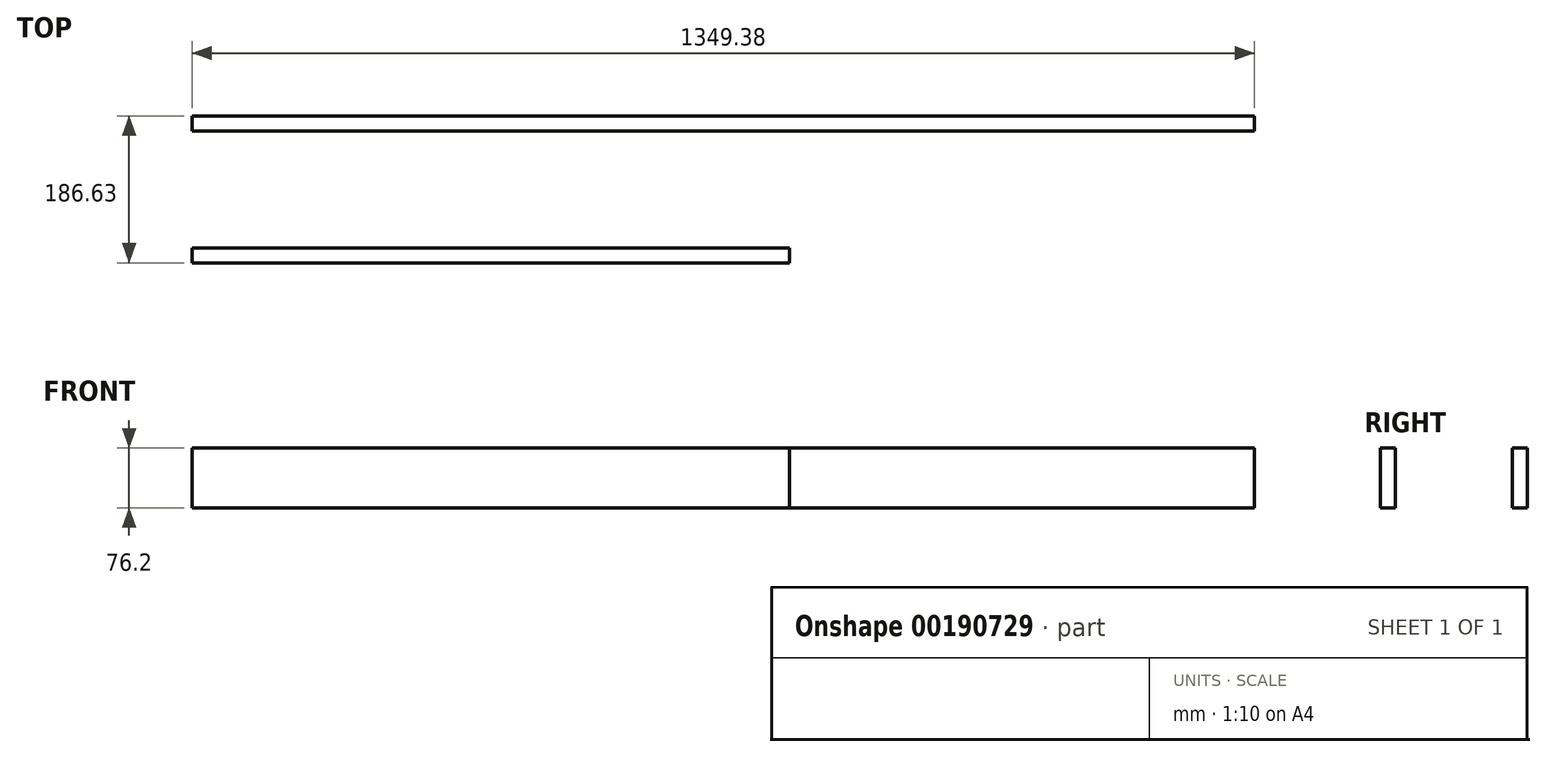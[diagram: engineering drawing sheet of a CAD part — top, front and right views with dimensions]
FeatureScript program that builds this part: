
annotation { "Feature Type Name" : "Feature", "Feature Type Description" : "" }
export const myFeature = defineFeature(function(context is Context, id is Id, definition is map)
    precondition{}
    {
        {
            var Q0;
            Q0=qCreatedBy(makeId("Right.planeOp"),FACE);
            var sketch = newSketch(context, id + "F0", { "sketchPlane" : qUnion([Q0])});
            skLineSegment(sketch, "E0.bottom", {"start": v(0, 0) * mm, "end": v(19.05, 0) * mm});
            skLineSegment(sketch, "E0.top", {"start": v(0, 76.2) * mm, "end": v(19.05, 76.2) * mm});
            skLineSegment(sketch, "E0.left", {"start": v(0, 0) * mm, "end": v(0, 76.2) * mm});
            skLineSegment(sketch, "E0.right", {"start": v(19.05, 0) * mm, "end": v(19.05, 76.2) * mm});
            skSolve(sketch);
        }
        {
            var Q0;
            Q0 = qSketchRegion(id + "F0", true);
            extrude(context, id + "F1", {"entities" : qUnion([Q0]), "depth" : 1349.38 * mm, "offsetDistance" : 25.4 * mm});
        }
        {
            var Q0;
            Q0=qCreatedBy(makeId("Right.planeOp"),FACE);
            var sketch = newSketch(context, id + "F2", { "sketchPlane" : qUnion([Q0])});
            skLineSegment(sketch, "E1.bottom", {"start": v(-167.58, 0) * mm, "end": v(-148.53, 0) * mm});
            skLineSegment(sketch, "E1.top", {"start": v(-167.58, 76.2) * mm, "end": v(-148.53, 76.2) * mm});
            skLineSegment(sketch, "E1.left", {"start": v(-167.58, 0) * mm, "end": v(-167.58, 76.2) * mm});
            skLineSegment(sketch, "E1.right", {"start": v(-148.53, 0) * mm, "end": v(-148.53, 76.2) * mm});
            skSolve(sketch);
        }
        {
            var Q0;
            Q0 = qSketchRegion(id + "F2", true);
            extrude(context, id + "F3", {"entities" : qUnion([Q0]), "depth" : 758.82 * mm});
        }
    });
